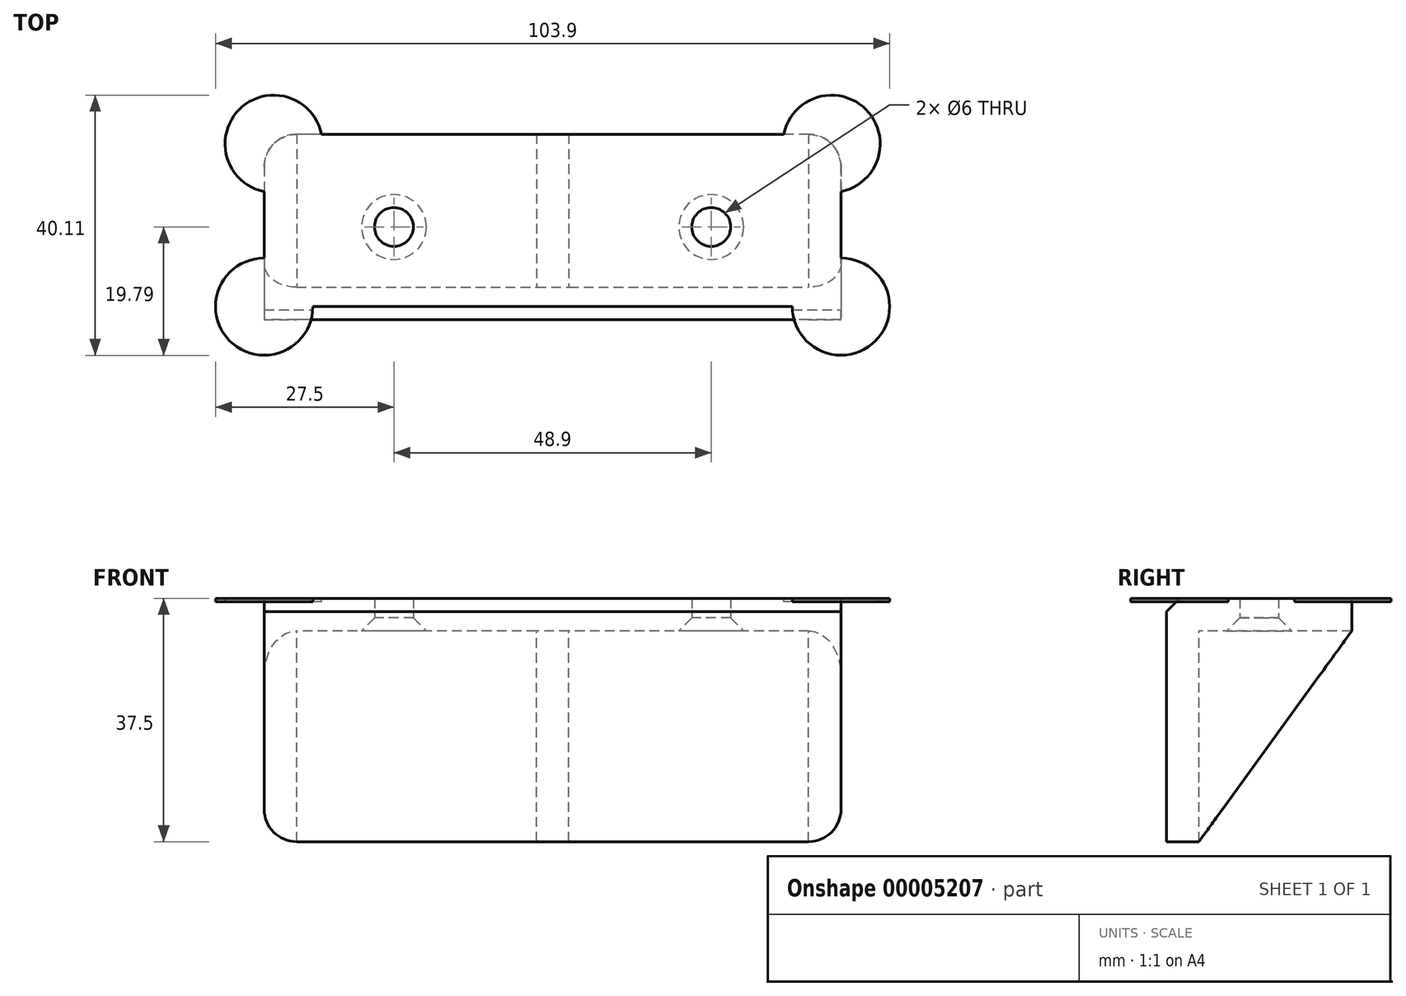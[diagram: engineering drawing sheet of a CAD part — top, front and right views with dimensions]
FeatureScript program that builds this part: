
annotation { "Feature Type Name" : "Feature", "Feature Type Description" : "" }
export const myFeature = defineFeature(function(context is Context, id is Id, definition is map)
    precondition{}
    {
        {
            var Q0;
            Q0=qCreatedBy(makeId("Top.planeOp"),FACE);
            var sketch = newSketch(context, id + "F0", { "sketchPlane" : qUnion([Q0])});
            skLineSegment(sketch, "E0.bottom", {"start": v(44.45, 14.29) * mm, "end": v(-44.45, 14.29) * mm});
            skLineSegment(sketch, "E0.top", {"start": v(44.45, -14.29) * mm, "end": v(-44.45, -14.29) * mm});
            skLineSegment(sketch, "E0.left", {"start": v(44.45, 14.29) * mm, "end": v(44.45, -14.29) * mm});
            skLineSegment(sketch, "E0.right", {"start": v(-44.45, 14.29) * mm, "end": v(-44.45, -14.29) * mm});
            skPoint(sketch, "E0.middle", {"position": v(0, 0) * mm});
            skLineSegment(sketch, "E1", {"start": v(-44.45, 0) * mm, "end": v(44.45, 0) * mm, "construction": true});
            skLineSegment(sketch, "E2", {"start": v(0, 14.29) * mm, "end": v(0, -14.29) * mm, "construction": true});
            skCircle(sketch, "E3", {"center": v(-24.45, 0) * mm, "radius": 3 * mm});
            skCircle(sketch, "E4.MirrorC", {"center": v(24.45, 0) * mm, "radius": 3 * mm});
            skSolve(sketch);
        }
        {
            var Q0;
            Q0 = qSketchRegion(id + "F0", true);
            extrude(context, id + "F1", {"entities" : qUnion([Q0]), "depth" : 5 * mm, "offsetDistance" : 25 * mm});
        }
        {
            var Q0;
            Q0=makeQuery(id+"F1.opExtrude","CAP_FACE",FACE,{"disambiguationData":[OSD([sQuery(id+"F0.wireOp",EDGE,"E0.bottom"),sQuery(id+"F0.wireOp",EDGE,"E0.top"),sQuery(id+"F0.wireOp",EDGE,"E0.left"),sQuery(id+"F0.wireOp",EDGE,"E0.right"),sQuery(id+"F0.wireOp",EDGE,"E3"),sQuery(id+"F0.wireOp",EDGE,"E4.MirrorC")])],"isStart":true});
            var sketch = newSketch(context, id + "F2", { "sketchPlane" : qUnion([Q0])});
            skLineSegment(sketch, "E5.bottom", {"start": v(-44.45, 14.29) * mm, "end": v(44.45, 14.29) * mm});
            skLineSegment(sketch, "E5.top", {"start": v(-44.45, 9.29) * mm, "end": v(44.45, 9.29) * mm});
            skLineSegment(sketch, "E5.left", {"start": v(-44.45, 14.29) * mm, "end": v(-44.45, 9.29) * mm});
            skLineSegment(sketch, "E5.right", {"start": v(44.45, 14.29) * mm, "end": v(44.45, 9.29) * mm});
            skSolve(sketch);
        }
        {
            var Q0;
            Q0 = qSketchRegion(id + "F2", true);
            extrude(context, id + "F3", {"entities" : qUnion([Q0]), "operationType" : NewBodyOperationType.ADD, "depth" : 32.5 * mm, "offsetDistance" : 25 * mm});
        }
        {
            var Q0;
            Q0=makeQuery(id+"F1.opExtrude","CAP_FACE",FACE,{"disambiguationData":[OSD([sQuery(id+"F0.wireOp",EDGE,"E0.bottom"),sQuery(id+"F0.wireOp",EDGE,"E0.top"),sQuery(id+"F0.wireOp",EDGE,"E0.left"),sQuery(id+"F0.wireOp",EDGE,"E0.right"),sQuery(id+"F0.wireOp",EDGE,"E3"),sQuery(id+"F0.wireOp",EDGE,"E4.MirrorC")])],"isStart":true});
            var sketch = newSketch(context, id + "F4", { "sketchPlane" : qUnion([Q0])});
            skLineSegment(sketch, "E6.bottom", {"start": v(44.45, -14.29) * mm, "end": v(39.45, -14.29) * mm});
            skLineSegment(sketch, "E6.top", {"start": v(44.45, 9.29) * mm, "end": v(39.45, 9.29) * mm});
            skLineSegment(sketch, "E6.left", {"start": v(44.45, -14.29) * mm, "end": v(44.45, 9.29) * mm});
            skLineSegment(sketch, "E6.right", {"start": v(39.45, -14.29) * mm, "end": v(39.45, 9.29) * mm});
            skLineSegment(sketch, "E7.bottom", {"start": v(-44.45, -14.29) * mm, "end": v(-39.45, -14.29) * mm});
            skLineSegment(sketch, "E7.top", {"start": v(-44.45, 9.29) * mm, "end": v(-39.45, 9.29) * mm});
            skLineSegment(sketch, "E7.left", {"start": v(-44.45, -14.29) * mm, "end": v(-44.45, 9.29) * mm});
            skLineSegment(sketch, "E7.right", {"start": v(-39.45, -14.29) * mm, "end": v(-39.45, 9.29) * mm});
            skLineSegment(sketch, "E8.bottom", {"start": v(2.5, -14.29) * mm, "end": v(-2.5, -14.29) * mm});
            skLineSegment(sketch, "E8.top", {"start": v(2.5, 9.29) * mm, "end": v(-2.5, 9.29) * mm});
            skLineSegment(sketch, "E8.left", {"start": v(2.5, -14.29) * mm, "end": v(2.5, 9.29) * mm});
            skLineSegment(sketch, "E8.right", {"start": v(-2.5, -14.29) * mm, "end": v(-2.5, 9.29) * mm});
            skLineSegment(sketch, "E9", {"start": v(0, 0) * mm, "end": v(0, -14.29) * mm, "construction": true});
            skSolve(sketch);
        }
        {
            var Q0;
            Q0 = qSketchRegion(id + "F4", true);
            var Q1;
            Q1=makeQuery(id+"F3.opExtrude","CAP_FACE",FACE,{"disambiguationData":[OSD([sQuery(id+"F2.wireOp",EDGE,"E5.bottom"),sQuery(id+"F2.wireOp",EDGE,"E5.top"),sQuery(id+"F2.wireOp",EDGE,"E5.left"),sQuery(id+"F2.wireOp",EDGE,"E5.right")])],"isStart":false});
            extrude(context, id + "F5", {"entities" : qUnion([Q0]), "operationType" : NewBodyOperationType.ADD, "endBound" : BoundingType.UP_TO_SURFACE, "depth" : 25 * mm, "endBoundEntityFace" : qUnion([Q1]), "offsetDistance" : 25 * mm});
        }
        {
            var Q0;
            Q0=makeQuery(id+"F5.opExtrude","CAP_EDGE",EDGE,{"disambiguationData":[OSD([sQuery(id+"F4.wireOp",EDGE,"E6.bottom")])],"isStart":false});
            var Q1;
            Q1=makeQuery(id+"F5.opExtrude","CAP_EDGE",EDGE,{"disambiguationData":[OSD([sQuery(id+"F4.wireOp",EDGE,"E8.bottom")])],"isStart":false});
            var Q2;
            Q2=makeQuery(id+"F5.opExtrude","CAP_EDGE",EDGE,{"disambiguationData":[OSD([sQuery(id+"F4.wireOp",EDGE,"E7.bottom")])],"isStart":false});
            chamfer(context, id + "F6", {"entities" : qUnion([Q0, Q1, Q2]), "chamferType" : ChamferType.TWO_OFFSETS, "width1" : 32.5 * mm, "oppositeDirection" : false, "width2" : 23.57 * mm, "tangentPropagation" : true});
        }
        {
            var Q0;
            Q0=makeQuery(id+"F5.boolean.opBoolean","MERGE",EDGE,{"derivedFrom":[makeQuery(id+"F1.opExtrude","SWEPT_EDGE",EDGE,{"disambiguationData":[OSD([sQuery(id+"F0.wireOp",EDGE,"E0.bottom"),sQuery(id+"F0.wireOp",EDGE,"E0.left")])]}),makeQuery(id+"F5.opExtrude","SWEPT_EDGE",EDGE,{"disambiguationData":[OSD([sQuery(id+"F4.wireOp",EDGE,"E6.bottom"),sQuery(id+"F4.wireOp",EDGE,"E6.left")])]})]});
            var Q1;
            Q1=makeQuery(id+"F5.boolean.opBoolean","MERGE",EDGE,{"derivedFrom":[makeQuery(id+"F1.opExtrude","SWEPT_EDGE",EDGE,{"disambiguationData":[OSD([sQuery(id+"F0.wireOp",EDGE,"E0.bottom"),sQuery(id+"F0.wireOp",EDGE,"E0.right")])]}),makeQuery(id+"F5.opExtrude","SWEPT_EDGE",EDGE,{"disambiguationData":[OSD([sQuery(id+"F4.wireOp",EDGE,"E7.bottom"),sQuery(id+"F4.wireOp",EDGE,"E7.left")])]})]});
            var Q2;
            Q2=makeQuery(id+"F5.boolean.opBoolean","MERGE",EDGE,{"derivedFrom":[makeQuery(id+"F3.opExtrude","CAP_EDGE",EDGE,{"disambiguationData":[OSD([sQuery(id+"F2.wireOp",EDGE,"E5.left")])],"isStart":false}),makeQuery(id+"F5.opExtrude","CAP_EDGE",EDGE,{"disambiguationData":[OSD([sQuery(id+"F4.wireOp",EDGE,"E7.left")])],"isStart":false})]});
            var Q3;
            Q3=makeQuery(id+"F5.boolean.opBoolean","MERGE",EDGE,{"derivedFrom":[makeQuery(id+"F3.opExtrude","CAP_EDGE",EDGE,{"disambiguationData":[OSD([sQuery(id+"F2.wireOp",EDGE,"E5.right")])],"isStart":false}),makeQuery(id+"F5.opExtrude","CAP_EDGE",EDGE,{"disambiguationData":[OSD([sQuery(id+"F4.wireOp",EDGE,"E6.left")])],"isStart":false})]});
            fillet(context, id + "F7", {"entities" : qUnion([Q0, Q1, Q2, Q3]), "radius" : 5 * mm, "tangentPropagation" : true, "allowEdgeOverflow" : false});
        }
        {
            var Q0;
            Q0=makeQuery(id+"F1.opExtrude","CAP_EDGE",EDGE,{"disambiguationData":[OSD([sQuery(id+"F0.wireOp",EDGE,"E0.top")])],"isStart":false});
            chamfer(context, id + "F8", {"entities" : qUnion([Q0]), "width" : 2 * mm, "tangentPropagation" : true});
        }
        {
            var Q0;
            Q0=makeQuery(id+"F1.opExtrude","CAP_EDGE",EDGE,{"disambiguationData":[OSD([sQuery(id+"F0.wireOp",EDGE,"E4.MirrorC")])],"isStart":true});
            var Q1;
            Q1=makeQuery(id+"F1.opExtrude","CAP_EDGE",EDGE,{"disambiguationData":[OSD([sQuery(id+"F0.wireOp",EDGE,"E3")])],"isStart":true});
            chamfer(context, id + "F9", {"entities" : qUnion([Q0, Q1]), "width" : 2 * mm, "tangentPropagation" : true});
        }
        {
            var Q0;
            Q0=makeQuery(id+"F1.opExtrude","CAP_FACE",FACE,{"disambiguationData":[OSD([sQuery(id+"F0.wireOp",EDGE,"E0.bottom"),sQuery(id+"F0.wireOp",EDGE,"E0.top"),sQuery(id+"F0.wireOp",EDGE,"E0.left"),sQuery(id+"F0.wireOp",EDGE,"E0.right"),sQuery(id+"F0.wireOp",EDGE,"E3"),sQuery(id+"F0.wireOp",EDGE,"E4.MirrorC")])],"isStart":false});
            var sketch = newSketch(context, id + "F10", { "sketchPlane" : qUnion([Q0])});
            skCircle(sketch, "E10", {"center": v(42.99, 12.82) * mm, "radius": 7.5 * mm});
            skCircle(sketch, "E11", {"center": v(44.45, -12.29) * mm, "radius": 7.5 * mm});
            skCircle(sketch, "E12", {"center": v(-44.45, -12.29) * mm, "radius": 7.5 * mm});
            skCircle(sketch, "E13", {"center": v(-42.99, 12.82) * mm, "radius": 7.5 * mm});
            skSolve(sketch);
        }
        {
            var Q0;
            Q0 = qSketchRegion(id + "F10", true);
            extrude(context, id + "F11", {"entities" : qUnion([Q0]), "operationType" : NewBodyOperationType.ADD, "oppositeDirection" : true, "depth" : 0.5 * mm, "offsetDistance" : 25 * mm});
        }
    });
